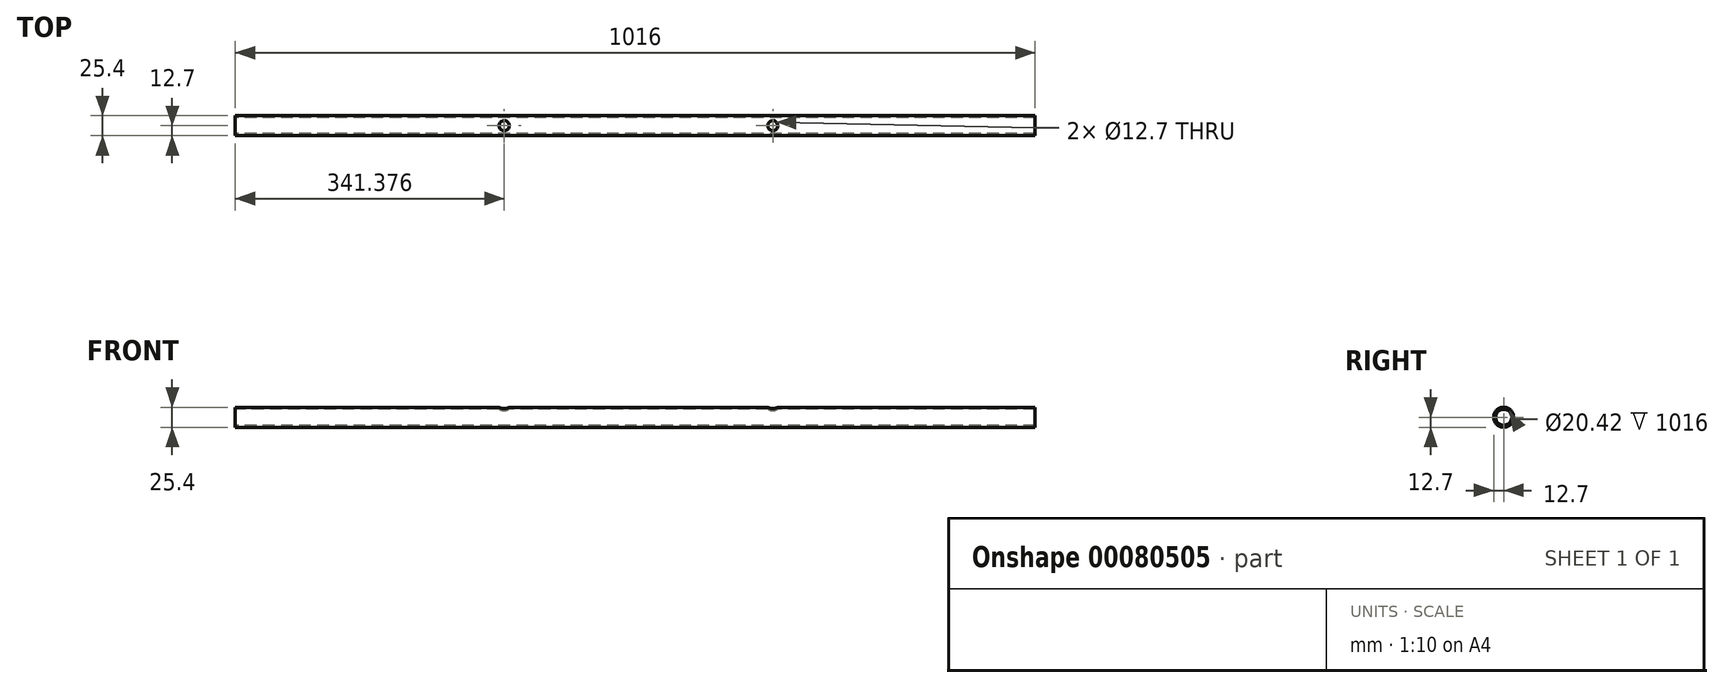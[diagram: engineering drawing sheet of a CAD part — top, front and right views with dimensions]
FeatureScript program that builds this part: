
annotation { "Feature Type Name" : "Feature", "Feature Type Description" : "" }
export const myFeature = defineFeature(function(context is Context, id is Id, definition is map)
    precondition{}
    {
        {
            var Q0;
            Q0=qCreatedBy(makeId("Right.planeOp"),FACE);
            var sketch = newSketch(context, id + "F0", { "sketchPlane" : qUnion([Q0])});
            skCircle(sketch, "E0", {"center": v(0, 0) * mm, "radius": 12.7 * mm});
            skCircle(sketch, "E1", {"center": v(0, 0) * mm, "radius": 10.21 * mm});
            skSolve(sketch);
        }
        {
            var Q0;
            Q0=makeQuery(id+"F0.imprint","IMPRINT",FACE,{"disambiguationData":[TD([[makeQuery(id+"F0.imprint","IMPRINT",EDGE,{"derivedFrom":sQuery(id+"F0.wireOp",EDGE,"E0")}),1.0]])]});
            extrude(context, id + "F1", {"entities" : qUnion([Q0]), "depth" : 1016 * mm});
        }
        {
            var Q0;
            Q0=qCreatedBy(makeId("Top.planeOp"),FACE);
            var sketch = newSketch(context, id + "F2", { "sketchPlane" : qUnion([Q0])});
            skCircle(sketch, "E2", {"center": v(341.38, 0) * mm, "radius": 6.35 * mm});
            skCircle(sketch, "E3", {"center": v(682.75, 0) * mm, "radius": 6.35 * mm});
            skCircle(sketch, "E4", {"center": v(1024.13, 0) * mm, "radius": 6.35 * mm});
            skCircle(sketch, "E5", {"center": v(1365.5, 0) * mm, "radius": 6.35 * mm});
            skSolve(sketch);
        }
        {
            var Q0;
            Q0 = qSketchRegion(id + "F2", true);
            extrude(context, id + "F3", {"entities" : qUnion([Q0]), "operationType" : NewBodyOperationType.REMOVE, "depth" : 25.4 * mm});
        }
    });
